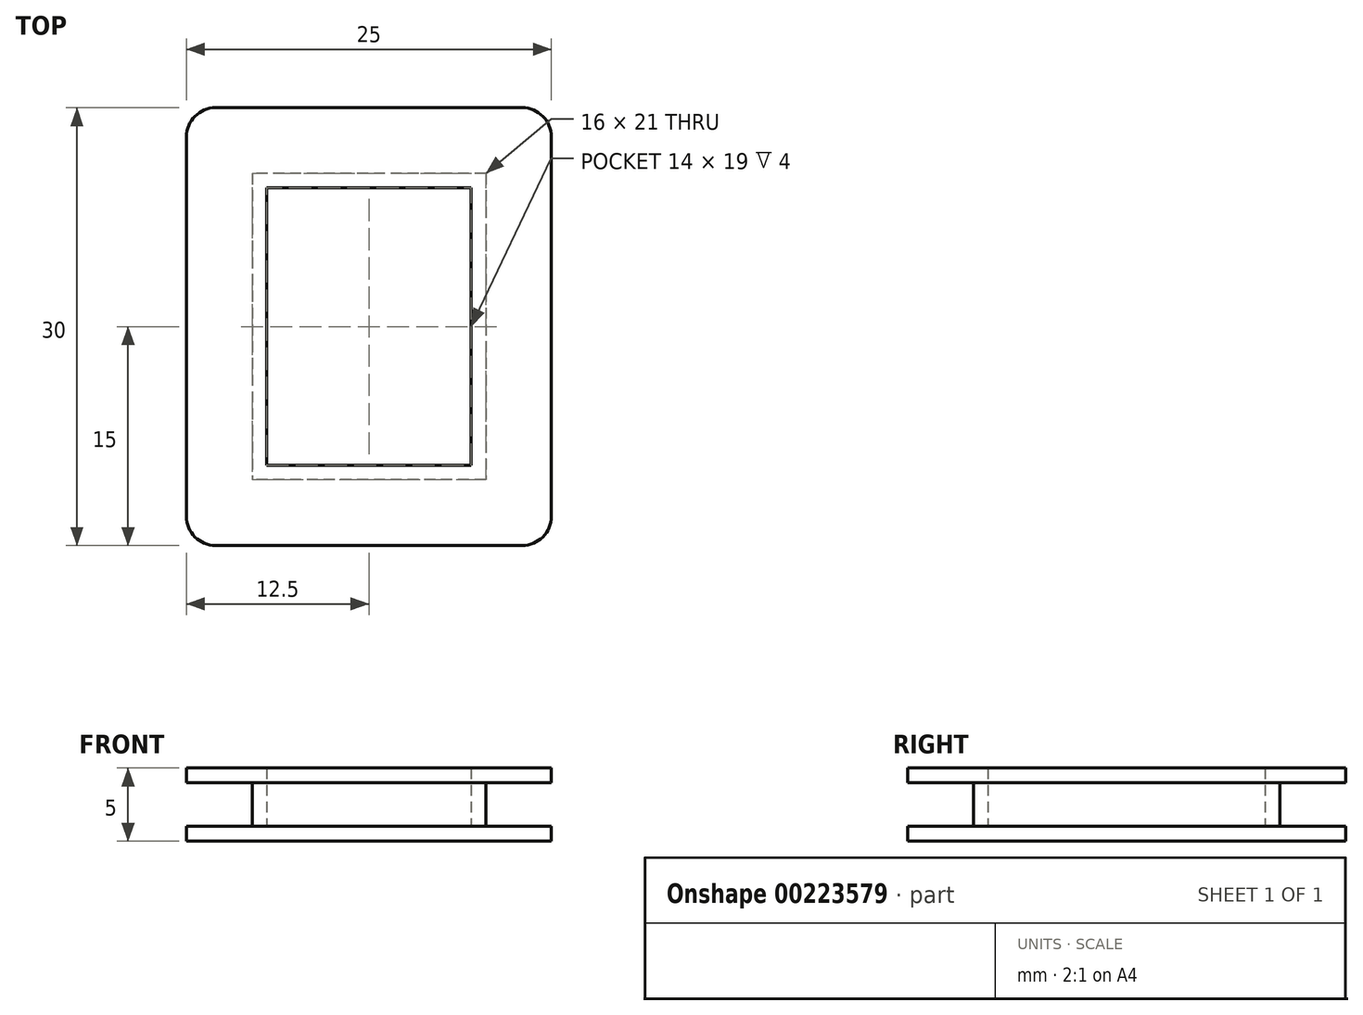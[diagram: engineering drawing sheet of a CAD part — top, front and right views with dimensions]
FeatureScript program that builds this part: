
annotation { "Feature Type Name" : "Feature", "Feature Type Description" : "" }
export const myFeature = defineFeature(function(context is Context, id is Id, definition is map)
    precondition{}
    {
        {
            var Q0;
            Q0=qCreatedBy(makeId("Top.planeOp"),FACE);
            var sketch = newSketch(context, id + "F0", { "sketchPlane" : qUnion([Q0])});
            skLineSegment(sketch, "E0.bottom", {"start": v(7.5, 10) * mm, "end": v(-7.5, 10) * mm, "construction": true});
            skLineSegment(sketch, "E0.top", {"start": v(7.5, -10) * mm, "end": v(-7.5, -10) * mm, "construction": true});
            skLineSegment(sketch, "E0.left", {"start": v(7.5, 10) * mm, "end": v(7.5, -10) * mm, "construction": true});
            skLineSegment(sketch, "E0.right", {"start": v(-7.5, 10) * mm, "end": v(-7.5, -10) * mm, "construction": true});
            skPoint(sketch, "E0.middle", {"position": v(0, 0) * mm});
            skLineSegment(sketch, "E1.bottom", {"start": v(10.5, 15) * mm, "end": v(-10.5, 15) * mm});
            skLineSegment(sketch, "E1.top", {"start": v(10.5, -15) * mm, "end": v(-10.5, -15) * mm});
            skLineSegment(sketch, "E1.left", {"start": v(12.5, 13) * mm, "end": v(12.5, -13) * mm});
            skLineSegment(sketch, "E1.right", {"start": v(-12.5, 13) * mm, "end": v(-12.5, -13) * mm});
            skPoint(sketch, "E2.visualSharp", {"position": v(-12.5, 15) * mm});
            skArc(sketch, "E2.filletArc", {"start": v(-10.5, 15) * mm, "mid": v(-11.91, 14.41) * mm, "end": v(-12.5, 13) * mm});
            skPoint(sketch, "E3.visualSharp", {"position": v(12.5, 15) * mm});
            skArc(sketch, "E3.filletArc", {"start": v(12.5, 13) * mm, "mid": v(11.91, 14.41) * mm, "end": v(10.5, 15) * mm});
            skPoint(sketch, "E4.visualSharp", {"position": v(12.5, -15) * mm});
            skArc(sketch, "E4.filletArc", {"start": v(10.5, -15) * mm, "mid": v(11.91, -14.41) * mm, "end": v(12.5, -13) * mm});
            skPoint(sketch, "E5.visualSharp", {"position": v(-12.5, -15) * mm});
            skArc(sketch, "E5.filletArc", {"start": v(-12.5, -13) * mm, "mid": v(-11.91, -14.41) * mm, "end": v(-10.5, -15) * mm});
            skSolve(sketch);
        }
        {
            var Q0;
            Q0=makeQuery(id+"F0.imprint","IMPRINT",FACE,{"disambiguationData":[TD([[makeQuery(id+"F0.imprint","IMPRINT",EDGE,{"derivedFrom":sQuery(id+"F0.wireOp",EDGE,"E1.bottom")}),1.0]])]});
            extrude(context, id + "F1", {"entities" : qUnion([Q0]), "depth" : 1 * mm});
        }
        {
            var Q0;
            Q0=makeQuery(id+"F1.opExtrude","CAP_FACE",FACE,{"disambiguationData":[OSD([sQuery(id+"F0.wireOp",EDGE,"E1.bottom"),sQuery(id+"F0.wireOp",EDGE,"E1.top"),sQuery(id+"F0.wireOp",EDGE,"E1.left"),sQuery(id+"F0.wireOp",EDGE,"E1.right"),sQuery(id+"F0.wireOp",EDGE,"E2.filletArc"),sQuery(id+"F0.wireOp",EDGE,"E3.filletArc"),sQuery(id+"F0.wireOp",EDGE,"E4.filletArc"),sQuery(id+"F0.wireOp",EDGE,"E5.filletArc")])],"isStart":false});
            var sketch = newSketch(context, id + "F2", { "sketchPlane" : qUnion([Q0])});
            skLineSegment(sketch, "E6.bottom", {"start": v(8, 10.5) * mm, "end": v(-8, 10.5) * mm});
            skLineSegment(sketch, "E6.top", {"start": v(8, -10.5) * mm, "end": v(-8, -10.5) * mm});
            skLineSegment(sketch, "E6.left", {"start": v(8, 10.5) * mm, "end": v(8, -10.5) * mm});
            skLineSegment(sketch, "E6.right", {"start": v(-8, 10.5) * mm, "end": v(-8, -10.5) * mm});
            skPoint(sketch, "E6.middle", {"position": v(0, 0) * mm});
            skLineSegment(sketch, "E7.0", {"start": v(7, 9.5) * mm, "end": v(-7, 9.5) * mm});
            skLineSegment(sketch, "E7.1", {"start": v(7, 9.5) * mm, "end": v(7, -9.5) * mm});
            skLineSegment(sketch, "E7.2", {"start": v(7, -9.5) * mm, "end": v(-7, -9.5) * mm});
            skLineSegment(sketch, "E7.3", {"start": v(-7, 9.5) * mm, "end": v(-7, -9.5) * mm});
            skSolve(sketch);
        }
        {
            var Q0;
            Q0 = qSketchRegion(id + "F2", true);
            extrude(context, id + "F3", {"entities" : qUnion([Q0]), "operationType" : NewBodyOperationType.ADD, "depth" : 3 * mm});
        }
        {
            var Q0;
            Q0=makeQuery(id+"F3.opExtrude","CAP_FACE",FACE,{"disambiguationData":[OSD([sQuery(id+"F2.wireOp",EDGE,"E6.bottom"),sQuery(id+"F2.wireOp",EDGE,"E6.top"),sQuery(id+"F2.wireOp",EDGE,"E6.left"),sQuery(id+"F2.wireOp",EDGE,"E6.right"),sQuery(id+"F2.wireOp",EDGE,"E7.0"),sQuery(id+"F2.wireOp",EDGE,"E7.1"),sQuery(id+"F2.wireOp",EDGE,"E7.2"),sQuery(id+"F2.wireOp",EDGE,"E7.3")])],"isStart":false});
            var sketch = newSketch(context, id + "F4", { "sketchPlane" : qUnion([Q0])});
            skLineSegment(sketch, "E8.bottom", {"start": v(7, 9.5) * mm, "end": v(-7, 9.5) * mm});
            skLineSegment(sketch, "E8.top", {"start": v(7, -9.5) * mm, "end": v(-7, -9.5) * mm});
            skLineSegment(sketch, "E8.left", {"start": v(7, 9.5) * mm, "end": v(7, -9.5) * mm});
            skLineSegment(sketch, "E8.right", {"start": v(-7, 9.5) * mm, "end": v(-7, -9.5) * mm});
            skPoint(sketch, "E8.middle", {"position": v(0, 0) * mm});
            skLineSegment(sketch, "E9.0", {"start": v(10.5, 15) * mm, "end": v(-10.5, 15) * mm});
            skArc(sketch, "E9.1", {"start": v(12.5, 13) * mm, "mid": v(11.91, 14.41) * mm, "end": v(10.5, 15) * mm});
            skArc(sketch, "E9.2", {"start": v(-10.5, 15) * mm, "mid": v(-11.91, 14.41) * mm, "end": v(-12.5, 13) * mm});
            skLineSegment(sketch, "E9.3", {"start": v(12.5, 13) * mm, "end": v(12.5, -13) * mm});
            skLineSegment(sketch, "E9.4", {"start": v(-12.5, 13) * mm, "end": v(-12.5, -13) * mm});
            skArc(sketch, "E9.5", {"start": v(-12.5, -13) * mm, "mid": v(-11.91, -14.41) * mm, "end": v(-10.5, -15) * mm});
            skLineSegment(sketch, "E9.6", {"start": v(10.5, -15) * mm, "end": v(-10.5, -15) * mm});
            skArc(sketch, "E9.7", {"start": v(10.5, -15) * mm, "mid": v(11.91, -14.41) * mm, "end": v(12.5, -13) * mm});
            skSolve(sketch);
        }
        {
            var Q0;
            Q0 = qSketchRegion(id + "F4", true);
            extrude(context, id + "F5", {"entities" : qUnion([Q0]), "operationType" : NewBodyOperationType.ADD, "depth" : 1 * mm});
        }
    });
